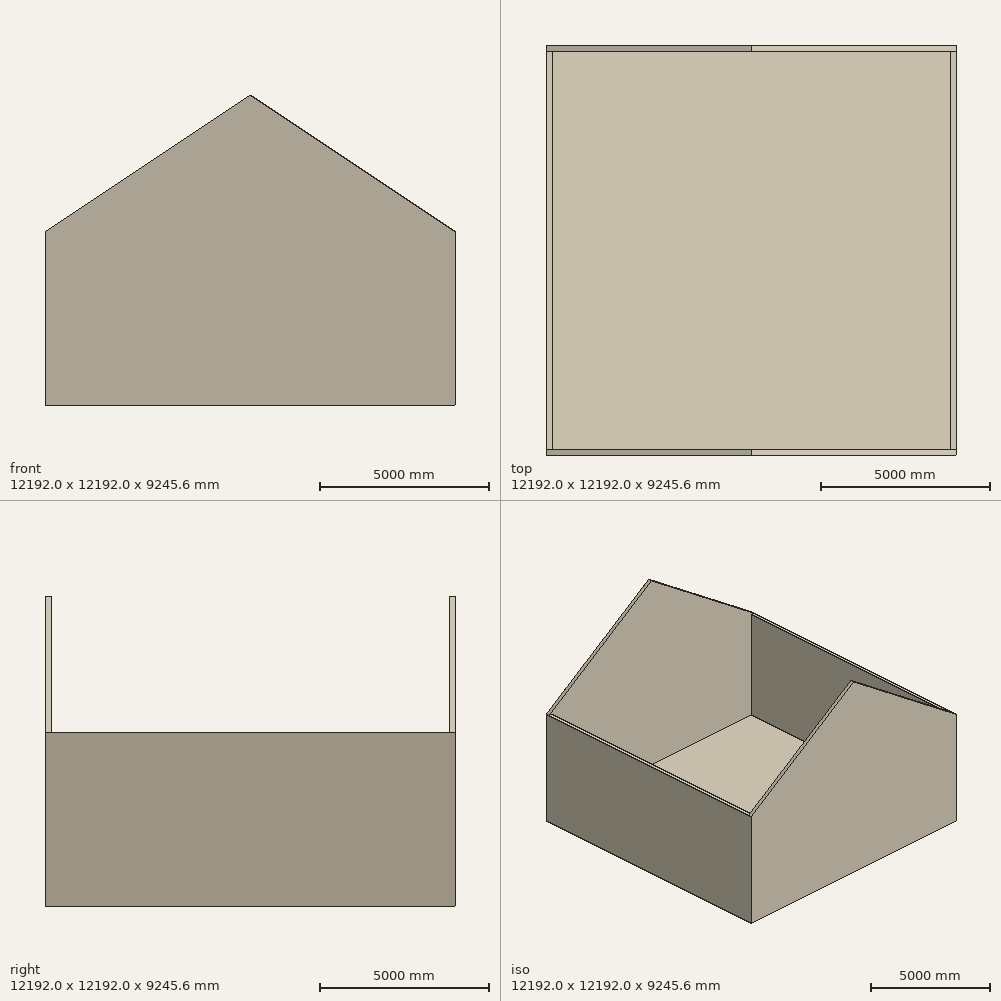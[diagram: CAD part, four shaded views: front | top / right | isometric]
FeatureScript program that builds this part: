
annotation { "Feature Type Name" : "Feature", "Feature Type Description" : "" }
export const myFeature = defineFeature(function(context is Context, id is Id, definition is map)
    precondition{}
    {
        {
            var Q0;
            Q0=qCreatedBy(makeId("Top.planeOp"),FACE);
            var sketch = newSketch(context, id + "F0", { "sketchPlane" : qUnion([Q0])});
            skLineSegment(sketch, "E0.bottom", {"start": v(0, 12192) * mm, "end": v(12192, 12192) * mm});
            skLineSegment(sketch, "E0.top", {"start": v(0, 0) * mm, "end": v(12192, 0) * mm});
            skLineSegment(sketch, "E0.left", {"start": v(0, 12192) * mm, "end": v(0, 0) * mm});
            skLineSegment(sketch, "E0.right", {"start": v(12192, 12192) * mm, "end": v(12192, 0) * mm});
            skSolve(sketch);
        }
        {
            var Q0;
            Q0=makeQuery(id+"F0.imprint","IMPRINT",FACE,{"disambiguationData":[TD([[makeQuery(id+"F0.imprint","IMPRINT",EDGE,{"derivedFrom":sQuery(id+"F0.wireOp",EDGE,"E0.bottom")}),-1.0]])]});
            extrude(context, id + "F1", {"entities" : qUnion([Q0]), "depth" : 304.8 * mm});
        }
        {
            var Q0;
            Q0=makeQuery(id+"F1.opExtrude","CAP_FACE",FACE,{"disambiguationData":[OSD([sQuery(id+"F0.wireOp",EDGE,"E0.bottom"),sQuery(id+"F0.wireOp",EDGE,"E0.top"),sQuery(id+"F0.wireOp",EDGE,"E0.left"),sQuery(id+"F0.wireOp",EDGE,"E0.right")])],"isStart":false});
            var sketch = newSketch(context, id + "F2", { "sketchPlane" : qUnion([Q0])});
            skLineSegment(sketch, "E1.0", {"start": v(0, 0) * mm, "end": v(12192, 0) * mm});
            skLineSegment(sketch, "E2.0", {"start": v(12192, 12192) * mm, "end": v(12192, 0) * mm});
            skLineSegment(sketch, "E3.0", {"start": v(0, 12192) * mm, "end": v(0, 0) * mm});
            skLineSegment(sketch, "E4.0", {"start": v(0, 12192) * mm, "end": v(12192, 12192) * mm});
            skLineSegment(sketch, "E5.0", {"start": v(165.1, 12026.9) * mm, "end": v(165.1, 165.1) * mm});
            skLineSegment(sketch, "E5.1", {"start": v(165.1, 12026.9) * mm, "end": v(12026.9, 12026.9) * mm});
            skLineSegment(sketch, "E5.2", {"start": v(12026.9, 12026.9) * mm, "end": v(12026.9, 165.1) * mm});
            skLineSegment(sketch, "E5.3", {"start": v(165.1, 165.1) * mm, "end": v(12026.9, 165.1) * mm});
            skSolve(sketch);
        }
        {
            var Q0;
            Q0 = qSketchRegion(id + "F2", true);
            extrude(context, id + "F3", {"entities" : qUnion([Q0]), "operationType" : NewBodyOperationType.ADD, "depth" : 4876.8 * mm});
        }
        {
            var Q0;
            Q0=makeQuery(id+"F3.boolean.opBoolean","MERGE",FACE,{"derivedFrom":[makeQuery(id+"F1.opExtrude","SWEPT_FACE",FACE,{"disambiguationData":[OSD([sQuery(id+"F0.wireOp",EDGE,"E0.top")])]}),makeQuery(id+"F3.opExtrude","SWEPT_FACE",FACE,{"disambiguationData":[OSD([sQuery(id+"F2.wireOp",EDGE,"E1.0")])]})]});
            var sketch = newSketch(context, id + "F4", { "sketchPlane" : qUnion([Q0])});
            skLineSegment(sketch, "E6", {"start": v(0, 5181.6) * mm, "end": v(6096, 9245.6) * mm});
            skLineSegment(sketch, "E7", {"start": v(6096, 9245.6) * mm, "end": v(12192, 5181.6) * mm});
            skLineSegment(sketch, "E8", {"start": v(6096, 9245.6) * mm, "end": v(5791.2, 9245.6) * mm, "construction": true});
            skLineSegment(sketch, "E9", {"start": v(5791.2, 9245.6) * mm, "end": v(5791.2, 9042.4) * mm, "construction": true});
            skSolve(sketch);
        }
        {
            var Q0;
            Q0=makeQuery(id+"F4.imprint","IMPRINT",FACE,{"disambiguationData":[TD([[makeQuery(id+"F4.imprint","IMPRINT",EDGE,{"derivedFrom":sQuery(id+"F4.wireOp",EDGE,"E6")}),-1.0]])]});
            var Q1;
            Q1=makeQuery(id+"F3.opExtrude","SWEPT_FACE",FACE,{"disambiguationData":[OSD([sQuery(id+"F2.wireOp",EDGE,"E5.3")])]});
            extrude(context, id + "F5", {"entities" : qUnion([Q0]), "endBound" : BoundingType.UP_TO_SURFACE, "oppositeDirection" : true, "endBoundEntityFace" : qUnion([Q1]), "depth" : 25.4 * mm});
        }
        {
            var Q0;
            Q0=makeQuery(id+"F3.boolean.opBoolean","MERGE",FACE,{"derivedFrom":[makeQuery(id+"F1.opExtrude","SWEPT_FACE",FACE,{"disambiguationData":[OSD([sQuery(id+"F0.wireOp",EDGE,"E0.top")])]}),makeQuery(id+"F3.opExtrude","SWEPT_FACE",FACE,{"disambiguationData":[OSD([sQuery(id+"F2.wireOp",EDGE,"E1.0")])]})]});
            var Q1;
            Q1=makeQuery(id+"F3.boolean.opBoolean","MERGE",FACE,{"derivedFrom":[makeQuery(id+"F1.opExtrude","SWEPT_FACE",FACE,{"disambiguationData":[OSD([sQuery(id+"F0.wireOp",EDGE,"E0.bottom")])]}),makeQuery(id+"F3.opExtrude","SWEPT_FACE",FACE,{"disambiguationData":[OSD([sQuery(id+"F2.wireOp",EDGE,"E4.0")])]})]});
            cPlane(context, id + "F6", {"entities" : qUnion([Q0, Q1]), "cplaneType" : CPlaneType.MID_PLANE, "offset" : 152.4 * mm, "width" : 152.4 * mm, "height" : 152.4 * mm});
        }
        {
            var Q0;
            Q0=makeQuery(id+"F5.opExtrude","SWEPT_BODY",BODY,{"disambiguationData":[OSD([sQuery(id+"F2.wireOp",EDGE,"E1.0"),sQuery(id+"F4.wireOp",EDGE,"E6"),sQuery(id+"F4.wireOp",EDGE,"E7")])]});
            var Q1;
            Q1=qCreatedBy(id+"F6.planeOp",FACE);
            mirror(context, id + "F7", {"operationType" : NewBodyOperationType.ADD, "entities" : qUnion([Q0]), "mirrorPlane" : qUnion([Q1])});
        }
    });
